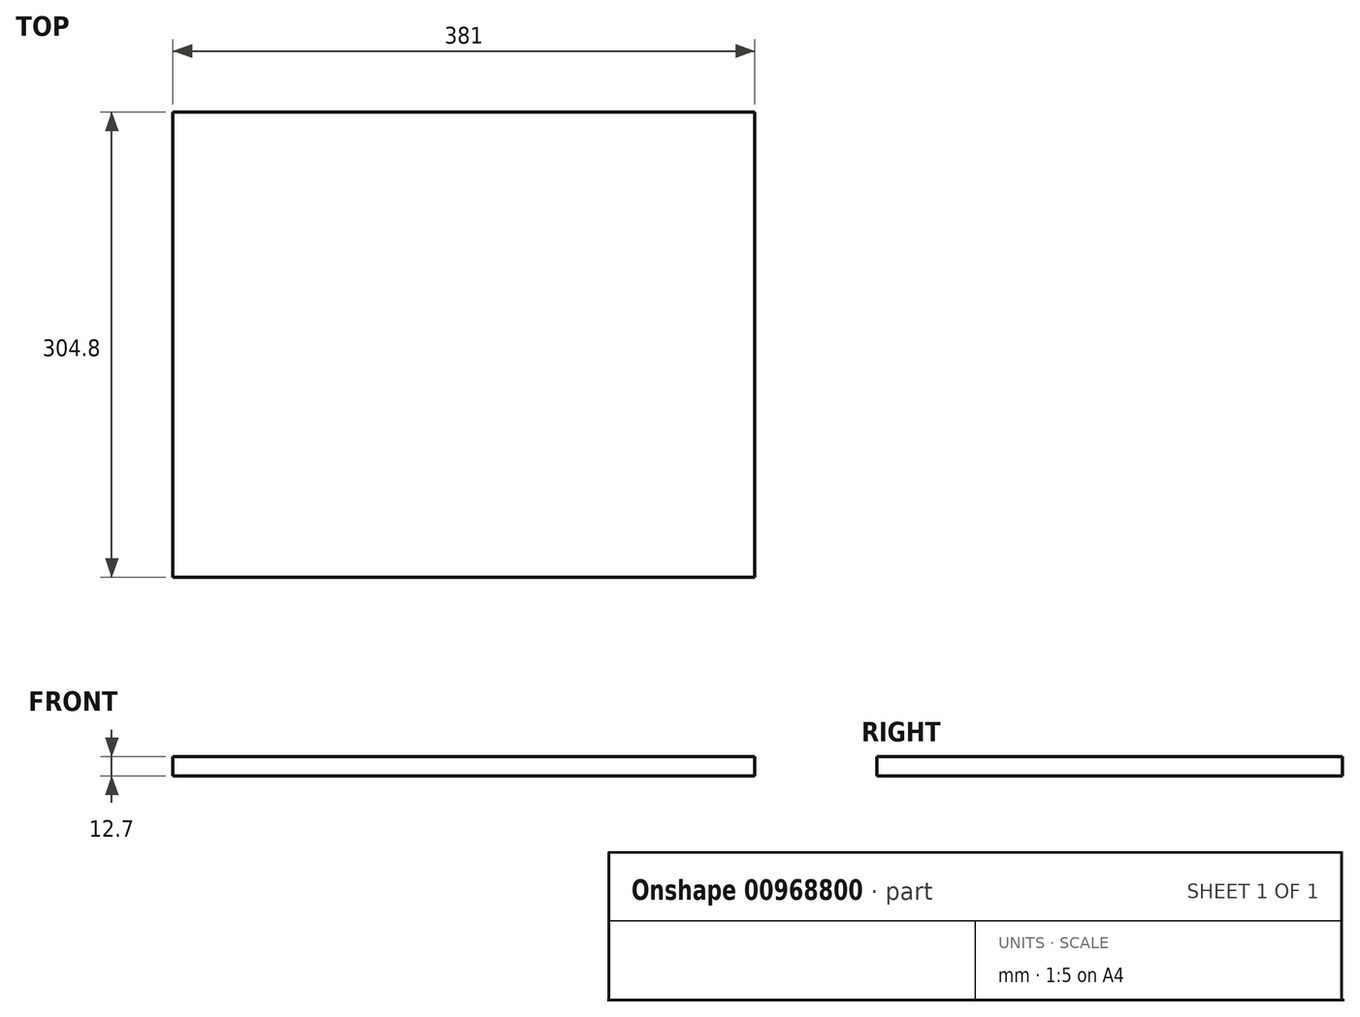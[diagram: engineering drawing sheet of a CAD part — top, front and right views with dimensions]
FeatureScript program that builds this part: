
annotation { "Feature Type Name" : "Feature", "Feature Type Description" : "" }
export const myFeature = defineFeature(function(context is Context, id is Id, definition is map)
    precondition{}
    {
        {
            var Q0;
            Q0=qCreatedBy(makeId("Top.planeOp"),FACE);
            var sketch = newSketch(context, id + "F0", { "sketchPlane" : qUnion([Q0])});
            skLineSegment(sketch, "E0.bottom", {"start": v(-151.3, 165.15) * mm, "end": v(229.7, 165.15) * mm});
            skLineSegment(sketch, "E0.top", {"start": v(-151.3, -139.65) * mm, "end": v(229.7, -139.65) * mm});
            skLineSegment(sketch, "E0.left", {"start": v(-151.3, 165.15) * mm, "end": v(-151.3, -139.65) * mm});
            skLineSegment(sketch, "E0.right", {"start": v(229.7, 165.15) * mm, "end": v(229.7, -139.65) * mm});
            skSolve(sketch);
        }
        {
            var Q0;
            Q0=makeQuery(id+"F0.imprint","IMPRINT",FACE,{"disambiguationData":[TD([[makeQuery(id+"F0.imprint","IMPRINT",EDGE,{"derivedFrom":sQuery(id+"F0.wireOp",EDGE,"E0.bottom")}),-1.0]])]});
            extrude(context, id + "F1", {"entities" : qUnion([Q0]), "depth" : 12.7 * mm, "offsetDistance" : 25.4 * mm});
        }
    });
